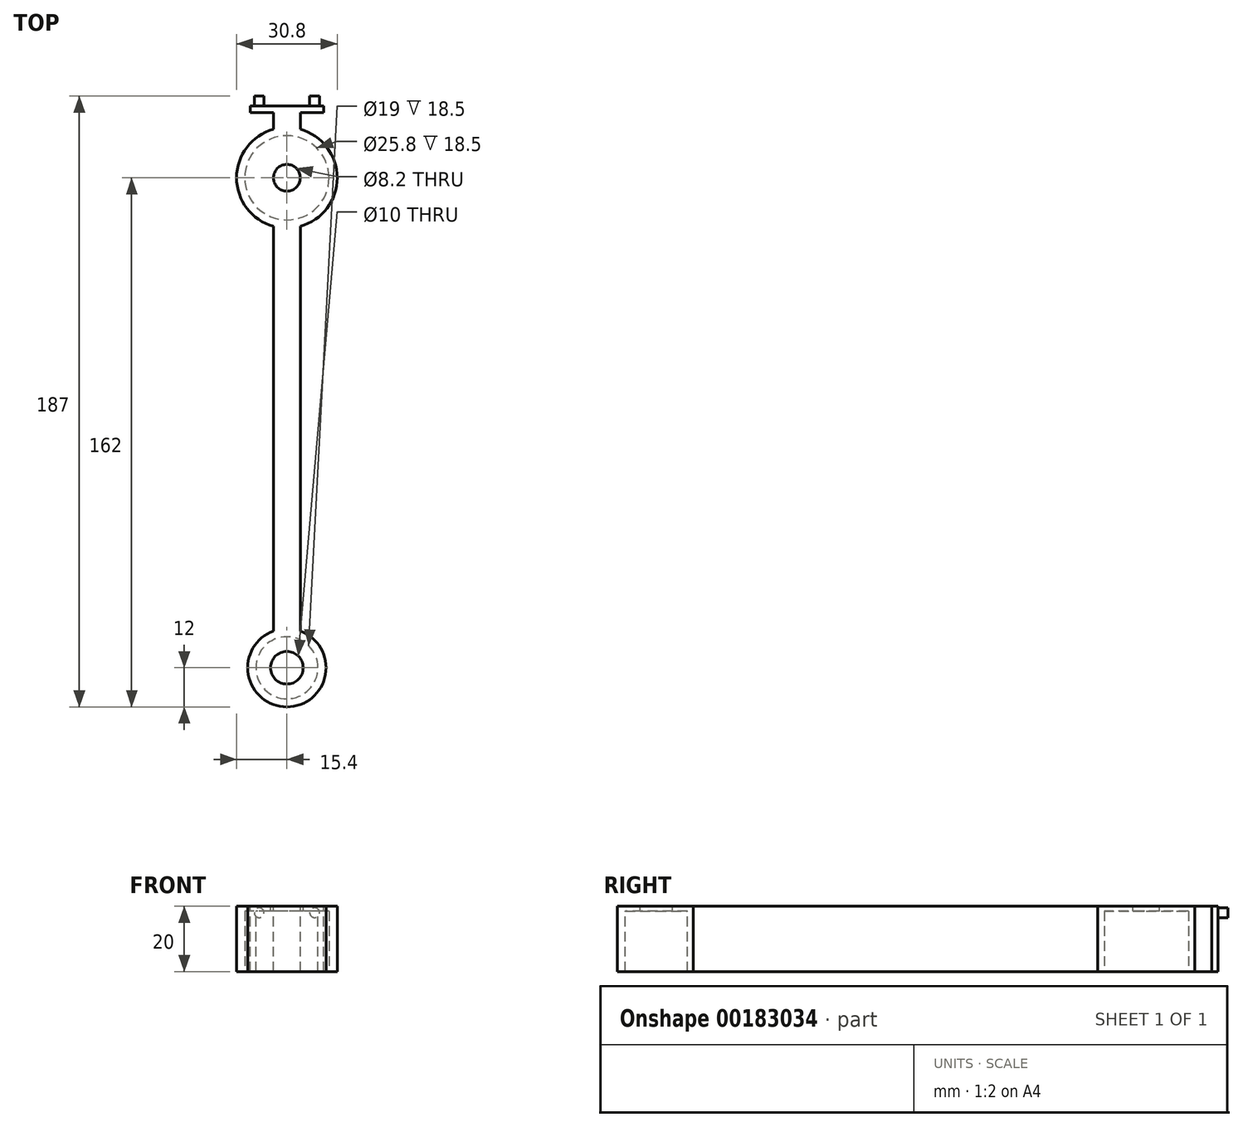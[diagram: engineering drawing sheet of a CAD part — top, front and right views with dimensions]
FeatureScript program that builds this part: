
annotation { "Feature Type Name" : "Feature", "Feature Type Description" : "" }
export const myFeature = defineFeature(function(context is Context, id is Id, definition is map)
    precondition{}
    {
        {
            var Q0;
            Q0=qCreatedBy(makeId("Top.planeOp"),FACE);
            var sketch = newSketch(context, id + "F0", { "sketchPlane" : qUnion([Q0])});
            skCircle(sketch, "E0", {"center": v(0, 0) * mm, "radius": 12.9 * mm});
            skCircle(sketch, "E1", {"center": v(0, 0) * mm, "radius": 15.4 * mm});
            skSolve(sketch);
        }
        {
            var Q0;
            Q0=makeQuery(id+"F0.imprint","IMPRINT",FACE,{"disambiguationData":[TD([[makeQuery(id+"F0.imprint","IMPRINT",EDGE,{"derivedFrom":sQuery(id+"F0.wireOp",EDGE,"E0")}),1.0]])]});
            var Q1;
            Q1=makeQuery(id+"F0.imprint","IMPRINT",FACE,{"disambiguationData":[TD([[makeQuery(id+"F0.imprint","IMPRINT",EDGE,{"derivedFrom":sQuery(id+"F0.wireOp",EDGE,"E0")}),-1.0]])]});
            extrude(context, id + "F1", {"entities" : qUnion([Q0, Q1]), "depth" : 20 * mm});
        }
        {
            var Q0;
            Q0=makeQuery(id+"F0.imprint","IMPRINT",FACE,{"disambiguationData":[TD([[makeQuery(id+"F0.imprint","IMPRINT",EDGE,{"derivedFrom":sQuery(id+"F0.wireOp",EDGE,"E0")}),1.0]])]});
            extrude(context, id + "F2", {"entities" : qUnion([Q0]), "operationType" : NewBodyOperationType.REMOVE, "depth" : 18.5 * mm});
        }
        {
            var Q0;
            Q0=makeQuery(id+"F1.opExtrude","CAP_FACE",FACE,{"disambiguationData":[OSD([sQuery(id+"F0.wireOp",EDGE,"E1")])],"isStart":false});
            var sketch = newSketch(context, id + "F3", { "sketchPlane" : qUnion([Q0])});
            skCircle(sketch, "E2", {"center": v(0, 0) * mm, "radius": 4.1 * mm});
            skSolve(sketch);
        }
        {
            var Q0;
            Q0=makeQuery(id+"F3.imprint","IMPRINT",FACE,{"disambiguationData":[TD([[makeQuery(id+"F3.imprint","IMPRINT",EDGE,{"derivedFrom":sQuery(id+"F3.wireOp",EDGE,"E2")}),1.0]])]});
            extrude(context, id + "F4", {"entities" : qUnion([Q0]), "operationType" : NewBodyOperationType.REMOVE, "oppositeDirection" : true, "depth" : 25 * mm});
        }
        {
            var Q0;
            Q0=makeQuery(id+"F1.opExtrude","CAP_FACE",FACE,{"disambiguationData":[OSD([sQuery(id+"F0.wireOp",EDGE,"E1")])],"isStart":false});
            var sketch = newSketch(context, id + "F5", { "sketchPlane" : qUnion([Q0])});
            skLineSegment(sketch, "E3", {"start": v(-4.1, 0) * mm, "end": v(4.1, 0) * mm});
            skLineSegment(sketch, "E4", {"start": v(4.1, 0) * mm, "end": v(4.1, -150) * mm});
            skLineSegment(sketch, "E5", {"start": v(-4.1, 0) * mm, "end": v(-4.1, -150) * mm});
            skLineSegment(sketch, "E6", {"start": v(-4.1, -150) * mm, "end": v(4.1, -150) * mm});
            skCircle(sketch, "E7", {"center": v(0, -150) * mm, "radius": 9.5 * mm});
            skCircle(sketch, "E8", {"center": v(0, -150) * mm, "radius": 12 * mm});
            skLineSegment(sketch, "E9.top", {"start": v(-4.1, 20) * mm, "end": v(4.1, 20) * mm});
            skLineSegment(sketch, "E9.left", {"start": v(-4.1, 0) * mm, "end": v(-4.1, 20) * mm});
            skLineSegment(sketch, "E9.right", {"start": v(4.1, 0) * mm, "end": v(4.1, 20) * mm});
            skSolve(sketch);
        }
        {
            var Q0;
            {var subQ0=sQuery(id+"F5.wireOp",EDGE,"E8");var subQ1=sQuery(id+"F5.wireOp",EDGE,"E4");var subQ2=makeQuery(id+"F5.imprint","INTERSECT",VERTEX,{"derivedFrom":[subQ1,subQ0]});Q0=makeQuery(id+"F5.imprint","IMPRINT",FACE,{"disambiguationData":[TD([[makeQuery(id+"F5.imprint","IMPRINT",EDGE,{"disambiguationData":[TD([[subQ2,1.0]])],"derivedFrom":subQ1}),-1.0]])]});}
            var Q1;
            {var subQ0=sQuery(id+"F5.wireOp",EDGE,"E8");var subQ1=sQuery(id+"F5.wireOp",EDGE,"E4");var subQ2=makeQuery(id+"F5.imprint","INTERSECT",VERTEX,{"derivedFrom":[subQ1,subQ0]});Q1=makeQuery(id+"F5.imprint","IMPRINT",FACE,{"disambiguationData":[TD([[makeQuery(id+"F5.imprint","IMPRINT",EDGE,{"disambiguationData":[TD([[subQ2,-1.0]])],"derivedFrom":subQ1}),-1.0]])]});}
            var Q2;
            {var subQ0=sQuery(id+"F5.wireOp",EDGE,"E8");var subQ1=sQuery(id+"F5.wireOp",EDGE,"E4");var subQ2=makeQuery(id+"F5.imprint","INTERSECT",VERTEX,{"derivedFrom":[subQ1,subQ0]});Q2=makeQuery(id+"F5.imprint","IMPRINT",FACE,{"disambiguationData":[TD([[makeQuery(id+"F5.imprint","IMPRINT",EDGE,{"disambiguationData":[TD([[subQ2,-1.0]])],"derivedFrom":subQ1}),1.0]])]});}
            var Q3;
            Q3=makeQuery(id+"F1.opExtrude","CAP_FACE",FACE,{"disambiguationData":[OSD([sQuery(id+"F0.wireOp",EDGE,"E1")])],"isStart":true});
            extrude(context, id + "F6", {"entities" : qUnion([Q0, Q1, Q2]), "operationType" : NewBodyOperationType.ADD, "endBound" : BoundingType.UP_TO_SURFACE, "oppositeDirection" : true, "endBoundEntityFace" : qUnion([Q3]), "depth" : 25 * mm});
        }
        {
            var Q0;
            {var subQ0=sQuery(id+"F0.wireOp",EDGE,"E1");Q0=makeQuery(id+"F6.boolean.opBoolean","MERGE",FACE,{"derivedFrom":[makeQuery(id+"F1.opExtrude","CAP_FACE",FACE,{"disambiguationData":[OSD([subQ0])],"isStart":false}),makeQuery(id+"F6.opExtrude","CAP_FACE",FACE,{"disambiguationData":[OSD([subQ0,sQuery(id+"F5.wireOp",EDGE,"E4"),sQuery(id+"F5.wireOp",EDGE,"E5"),sQuery(id+"F5.wireOp",EDGE,"E7"),sQuery(id+"F5.wireOp",EDGE,"E8")])],"isStart":true})]});}
            var sketch = newSketch(context, id + "F7", { "sketchPlane" : qUnion([Q0])});
            skCircle(sketch, "E10", {"center": v(0, -150) * mm, "radius": 5 * mm});
            skSolve(sketch);
        }
        {
            var Q0;
            Q0=makeQuery(id+"F7.imprint","IMPRINT",FACE,{"disambiguationData":[TD([[makeQuery(id+"F7.imprint","IMPRINT",EDGE,{"derivedFrom":sQuery(id+"F7.wireOp",EDGE,"E10")}),-1.0]])]});
            var Q1;
            Q1=makeQuery(id+"F2.boolean.opBoolean","COPY",FACE,{"derivedFrom":makeQuery(id+"F2.opExtrude","CAP_FACE",FACE,{"disambiguationData":[OSD([sQuery(id+"F0.wireOp",EDGE,"E0")])],"isStart":false})});
            extrude(context, id + "F8", {"entities" : qUnion([Q0]), "operationType" : NewBodyOperationType.ADD, "endBound" : BoundingType.UP_TO_SURFACE, "oppositeDirection" : true, "endBoundEntityFace" : qUnion([Q1]), "depth" : 1.5 * mm});
        }
        {
            var Q0;
            {var subQ0=sQuery(id+"F5.wireOp",EDGE,"E9.top");Q0=makeQuery(id+"F5.imprint","IMPRINT",FACE,{"disambiguationData":[TD([[makeQuery(id+"F5.imprint","IMPRINT",EDGE,{"derivedFrom":subQ0}),-1.0]])]});}
            var Q1;
            {var subQ0=sQuery(id+"F0.wireOp",EDGE,"E1");Q1=makeQuery(id+"F6.boolean.opBoolean","MERGE",FACE,{"derivedFrom":[makeQuery(id+"F1.opExtrude","CAP_FACE",FACE,{"disambiguationData":[OSD([subQ0])],"isStart":true}),makeQuery(id+"F6.opExtrude","CAP_FACE",FACE,{"disambiguationData":[OSD([subQ0])],"isStart":false})]});}
            extrude(context, id + "F9", {"entities" : qUnion([Q0]), "operationType" : NewBodyOperationType.ADD, "endBound" : BoundingType.UP_TO_SURFACE, "oppositeDirection" : true, "endBoundEntityFace" : qUnion([Q1]), "depth" : 25 * mm});
        }
        {
            var Q0;
            Q0=makeQuery(id+"F9.opExtrude","SWEPT_FACE",FACE,{"disambiguationData":[OSD([sQuery(id+"F5.wireOp",EDGE,"E9.top")])]});
            var sketch = newSketch(context, id + "F10", { "sketchPlane" : qUnion([Q0])});
            skLineSegment(sketch, "E11", {"start": v(0, 0) * mm, "end": v(12.5, 0) * mm, "construction": true});
            skLineSegment(sketch, "E12", {"start": v(0, 20) * mm, "end": v(-12.5, 20) * mm, "construction": true});
            skLineSegment(sketch, "E13.bottom", {"start": v(12.5, 0) * mm, "end": v(-12.5, 0) * mm});
            skLineSegment(sketch, "E13.top", {"start": v(12.5, 20) * mm, "end": v(-12.5, 20) * mm});
            skLineSegment(sketch, "E13.left", {"start": v(12.5, 0) * mm, "end": v(12.5, 20) * mm});
            skLineSegment(sketch, "E13.right", {"start": v(-12.5, 0) * mm, "end": v(-12.5, 20) * mm});
            skSolve(sketch);
        }
        {
            var Q0;
            {var subQ2=sQuery(id+"F10.wireOp",EDGE,"E13.right");Q0=makeQuery(id+"F10.imprint","IMPRINT",FACE,{"disambiguationData":[TD([[makeQuery(id+"F10.imprint","IMPRINT",EDGE,{"derivedFrom":subQ2}),-1.0]])]});}
            var Q1;
            {var subQ2=sQuery(id+"F10.wireOp",EDGE,"E13.left");Q1=makeQuery(id+"F10.imprint","IMPRINT",FACE,{"disambiguationData":[TD([[makeQuery(id+"F10.imprint","IMPRINT",EDGE,{"derivedFrom":subQ2}),1.0]])]});}
            var Q2;
            {var subQ1=sQuery(id+"F5.wireOp",EDGE,"E9.top");var subQ2=makeQuery(id+"F9.opExtrude","SWEPT_EDGE",EDGE,{"disambiguationData":[OSD([subQ1,sQuery(id+"F5.wireOp",EDGE,"E9.left")])]});Q2=makeQuery(id+"F10.imprint","IMPRINT",FACE,{"disambiguationData":[TD([[makeQuery(id+"F10.imprint","IMPRINT",EDGE,{"derivedFrom":subQ2}),1.0]])]});}
            extrude(context, id + "F11", {"entities" : qUnion([Q0, Q1, Q2]), "operationType" : NewBodyOperationType.ADD, "depth" : 2 * mm});
        }
        {
            var Q0;
            Q0=makeQuery(id+"F11.opExtrude","CAP_FACE",FACE,{"disambiguationData":[OSD([sQuery(id+"F10.wireOp",EDGE,"E13.bottom"),sQuery(id+"F10.wireOp",EDGE,"E13.top"),sQuery(id+"F10.wireOp",EDGE,"E13.left"),sQuery(id+"F10.wireOp",EDGE,"E13.right")])],"isStart":false});
            var sketch = newSketch(context, id + "F12", { "sketchPlane" : qUnion([Q0])});
            skLineSegment(sketch, "E14", {"start": v(-12.5, 20) * mm, "end": v(-12.5, 18) * mm, "construction": true});
            skLineSegment(sketch, "E15", {"start": v(-12.5, 18) * mm, "end": v(-8.5, 18) * mm, "construction": true});
            skCircle(sketch, "E16", {"center": v(-8.5, 18) * mm, "radius": 1.5 * mm});
            skLineSegment(sketch, "E17", {"start": v(12.5, 18) * mm, "end": v(8.5, 18) * mm, "construction": true});
            skCircle(sketch, "E18", {"center": v(8.5, 18) * mm, "radius": 1.5 * mm});
            skSolve(sketch);
        }
        {
            var Q0;
            Q0=makeQuery(id+"F12.imprint","IMPRINT",FACE,{"disambiguationData":[TD([[makeQuery(id+"F12.imprint","IMPRINT",EDGE,{"derivedFrom":sQuery(id+"F12.wireOp",EDGE,"E16")}),1.0]])]});
            var Q1;
            Q1=makeQuery(id+"F12.imprint","IMPRINT",FACE,{"disambiguationData":[TD([[makeQuery(id+"F12.imprint","IMPRINT",EDGE,{"derivedFrom":sQuery(id+"F12.wireOp",EDGE,"E18")}),1.0]])]});
            extrude(context, id + "F13", {"entities" : qUnion([Q0, Q1]), "operationType" : NewBodyOperationType.ADD, "depth" : 3 * mm});
        }
        {
            var Q0;
            Q0=makeQuery(id+"F11.opExtrude","SWEPT_FACE",FACE,{"disambiguationData":[OSD([sQuery(id+"F10.wireOp",EDGE,"E13.right")])]});
            extrude(context, id + "F14", {"entities" : qUnion([Q0]), "operationType" : NewBodyOperationType.REMOVE, "oppositeDirection" : true, "depth" : 1.25 * mm});
        }
        {
            var Q0;
            Q0=makeQuery(id+"F11.opExtrude","SWEPT_FACE",FACE,{"disambiguationData":[OSD([sQuery(id+"F10.wireOp",EDGE,"E13.left")])]});
            extrude(context, id + "F15", {"entities" : qUnion([Q0]), "operationType" : NewBodyOperationType.REMOVE, "oppositeDirection" : true, "depth" : 1.25 * mm});
        }
    });
